annotation { "Feature Type Name" : "Feature", "Feature Type Description" : "" }
export const myFeature = defineFeature(function(context is Context, id is Id, definition is map)
    precondition{}
    {
        {
            var Q0;
            Q0=qCreatedBy(makeId("Top.planeOp"),FACE);
            var sketch = newSketch(context, id + "F0", { "sketchPlane" : qUnion([Q0])});
            skLineSegment(sketch, "E0.bottom", {"start": v(990.6, -508) * mm, "end": v(-990.6, -508) * mm});
            skLineSegment(sketch, "E0.top", {"start": v(990.6, 508) * mm, "end": v(664.8, 508) * mm});
            skLineSegment(sketch, "E0.left", {"start": v(990.6, -508) * mm, "end": v(990.6, -50.8) * mm});
            skLineSegment(sketch, "E0.right", {"start": v(-990.6, -508) * mm, "end": v(-990.6, 508) * mm});
            skPoint(sketch, "E0.middle", {"position": v(0, 0) * mm});
            skLineSegment(sketch, "E1", {"start": v(-706.8, 508) * mm, "end": v(-706.8, 0) * mm});
            skLineSegment(sketch, "E2", {"start": v(-706.8, 0) * mm, "end": v(664.8, 0) * mm});
            skLineSegment(sketch, "E3", {"start": v(664.8, 0) * mm, "end": v(664.8, 508) * mm});
            skLineSegment(sketch, "E4.trimOffspring", {"start": v(-706.8, 508) * mm, "end": v(-990.6, 508) * mm});
            skArc(sketch, "E5", {"start": v(1069.63, -50.8) * mm, "mid": v(1980.5, 25.44) * mm, "end": v(1066.8, 0) * mm});
            skLineSegment(sketch, "E6", {"start": v(1069.63, -50.8) * mm, "end": v(990.6, -50.8) * mm});
            skLineSegment(sketch, "E7", {"start": v(1066.8, 0) * mm, "end": v(990.6, 0) * mm});
            skLineSegment(sketch, "E8.trimOffspring", {"start": v(990.6, 0) * mm, "end": v(990.6, 508) * mm});
            skSolve(sketch);
        }
        {
            var Q0;
            Q0 = qSketchRegion(id + "F0", true);
            extrude(context, id + "F1", {"entities" : qUnion([Q0]), "oppositeDirection" : true, "depth" : 1219.2 * mm, "offsetDistance" : 25.4 * mm});
        }
        {
            var Q0;
            Q0=makeQuery(id+"F1.opExtrude","CAP_FACE",FACE,{"disambiguationData":[OSD([sQuery(id+"F0.wireOp",EDGE,"E0.bottom"),sQuery(id+"F0.wireOp",EDGE,"E0.top"),sQuery(id+"F0.wireOp",EDGE,"E0.left"),sQuery(id+"F0.wireOp",EDGE,"E0.right"),sQuery(id+"F0.wireOp",EDGE,"E1"),sQuery(id+"F0.wireOp",EDGE,"E2"),sQuery(id+"F0.wireOp",EDGE,"E3"),sQuery(id+"F0.wireOp",EDGE,"E4.trimOffspring")])],"isStart":true});
            var sketch = newSketch(context, id + "F2", { "sketchPlane" : qUnion([Q0])});
            skText(sketch, "E9", { "text": "Coffee Bar", "fontName": "OpenSans-Regular.ttf"});
            const initialGuessF2  = {"E9": [-0.7068, -0.24745, 1, 0, 0.24745]};
            skSetInitialGuess(sketch, initialGuessF2);
            skSolve(sketch);
        }
        {
            var Q0;
            Q0 = qSketchRegion(id + "F2", true);
            extrude(context, id + "F3", {"entities" : qUnion([Q0]), "operationType" : NewBodyOperationType.ADD, "depth" : 25.4 * mm, "offsetDistance" : 25.4 * mm});
        }
        {
            var Q0;
            {var subQ29=sQuery(id+"F0.wireOp",EDGE,"E0.top");var subQ30=sQuery(id+"F0.wireOp",EDGE,"E0.bottom");var subQ31=sQuery(id+"F0.wireOp",EDGE,"E1");var subQ34=sQuery(id+"F0.wireOp",EDGE,"E2");var subQ36=sQuery(id+"F0.wireOp",EDGE,"E3");var subQ38=sQuery(id+"F0.wireOp",EDGE,"E4.trimOffspring");var subQ39=sQuery(id+"F0.wireOp",EDGE,"E0.left");var subQ41=sQuery(id+"F0.wireOp",EDGE,"E0.right");Q0=makeQuery(id+"F3.boolean.opBoolean","SPLIT",FACE,{"disambiguationData":[TD([makeQuery(id+"F1.opExtrude","SWEPT_FACE",FACE,{"disambiguationData":[OSD([subQ30])]})])],"derivedFrom":makeQuery(id+"F1.opExtrude","CAP_FACE",FACE,{"disambiguationData":[OSD([subQ30,subQ29,subQ39,subQ41,subQ31,subQ34,subQ36,subQ38])],"isStart":true})});}
            var sketch = newSketch(context, id + "F4", { "sketchPlane" : qUnion([Q0])});
            skCircle(sketch, "E10", {"center": v(1414.86, 0) * mm, "radius": 457.2 * mm});
            skLineSegment(sketch, "E11", {"start": v(1414.86, 0) * mm, "end": v(990.6, -279.4) * mm, "construction": true});
            skSolve(sketch);
        }
        {
            var Q0;
            Q0 = qSketchRegion(id + "F4", true);
            extrude(context, id + "F5", {"entities" : qUnion([Q0]), "oppositeDirection" : true, "depth" : 1016 * mm, "offsetDistance" : 25.4 * mm, "hasDraft" : true, "draftAngle" : 12 * degree, "draftPullDirection" : true});
        }
        {
            var Q0;
            Q0=makeQuery(id+"F5.opExtrude","SWEPT_BODY",BODY,{"disambiguationData":[OSD([sQuery(id+"F4.wireOp",EDGE,"E10")])]});
            deleteBodies(context, id + "F6", {"entities" : qUnion([Q0])});
        }
    });